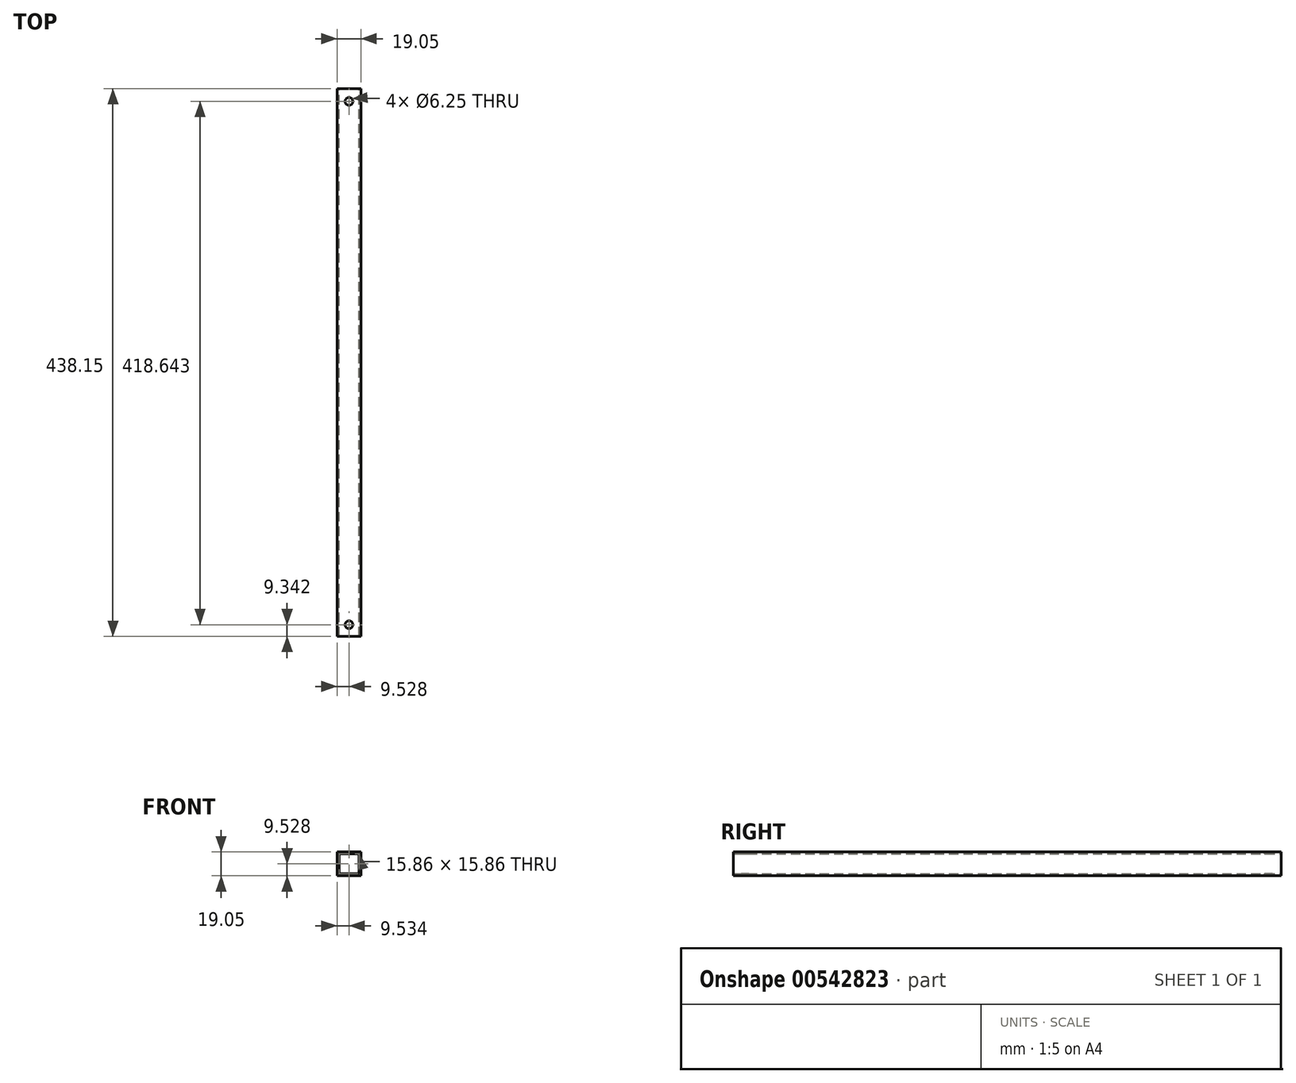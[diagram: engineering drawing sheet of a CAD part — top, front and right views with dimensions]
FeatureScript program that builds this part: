
annotation { "Feature Type Name" : "Feature", "Feature Type Description" : "" }
export const myFeature = defineFeature(function(context is Context, id is Id, definition is map)
    precondition{}
    {
        {
            var Q0;
            Q0=qCreatedBy(makeId("Front.planeOp"),FACE);
            var sketch = newSketch(context, id + "F0", { "sketchPlane" : qUnion([Q0])});
            skLineSegment(sketch, "E0.bottom", {"start": v(-8.48, 5.82) * mm, "end": v(7.39, 5.82) * mm});
            skLineSegment(sketch, "E0.top", {"start": v(-8.48, -10.04) * mm, "end": v(7.39, -10.04) * mm});
            skLineSegment(sketch, "E0.left", {"start": v(-8.48, 5.82) * mm, "end": v(-8.48, -10.04) * mm});
            skLineSegment(sketch, "E0.right", {"start": v(7.39, 5.82) * mm, "end": v(7.39, -10.04) * mm});
            skLineSegment(sketch, "E1.bottom", {"start": v(-10.08, 7.4) * mm, "end": v(8.97, 7.4) * mm});
            skLineSegment(sketch, "E1.top", {"start": v(-10.08, -11.64) * mm, "end": v(8.97, -11.64) * mm});
            skLineSegment(sketch, "E1.left", {"start": v(-10.08, 7.4) * mm, "end": v(-10.08, -11.64) * mm});
            skLineSegment(sketch, "E1.right", {"start": v(8.97, 7.4) * mm, "end": v(8.97, -11.64) * mm});
            skSolve(sketch);
        }
        {
            var Q0;
            Q0=qSketchRegion(id+"F0",true);
            extrude(context, id + "F1", {"entities" : qUnion([Q0]), "depth" : 438.15 * mm});
        }
        {
            var Q0;
            Q0=makeQuery(id+"F1.opExtrude","SWEPT_FACE",FACE,{"disambiguationData":[OSD([sQuery(id+"F0.wireOp",EDGE,"E1.bottom")])]});
            var sketch = newSketch(context, id + "F2", { "sketchPlane" : qUnion([Q0])});
            skCircle(sketch, "E2", {"center": v(-0.55, -428.8) * mm, "radius": 3.12 * mm});
            skCircle(sketch, "E3", {"center": v(-0.55, -10.17) * mm, "radius": 3.12 * mm});
            skSolve(sketch);
        }
        {
            var Q0;
            Q0=makeQuery(id+"F2.imprint","IMPRINT",FACE,{"disambiguationData":[TD([[makeQuery(id+"F2.imprint","IMPRINT",EDGE,{"derivedFrom":sQuery(id+"F2.wireOp",EDGE,"E3")}),1.0]])]});
            var Q1;
            Q1=makeQuery(id+"F2.imprint","IMPRINT",FACE,{"disambiguationData":[TD([[makeQuery(id+"F2.imprint","IMPRINT",EDGE,{"derivedFrom":sQuery(id+"F2.wireOp",EDGE,"E2")}),1.0]])]});
            extrude(context, id + "F3", {"entities" : qUnion([Q0, Q1]), "operationType" : NewBodyOperationType.REMOVE, "endBound" : BoundingType.THROUGH_ALL, "oppositeDirection" : true, "depth" : 12.7 * mm});
        }
    });
